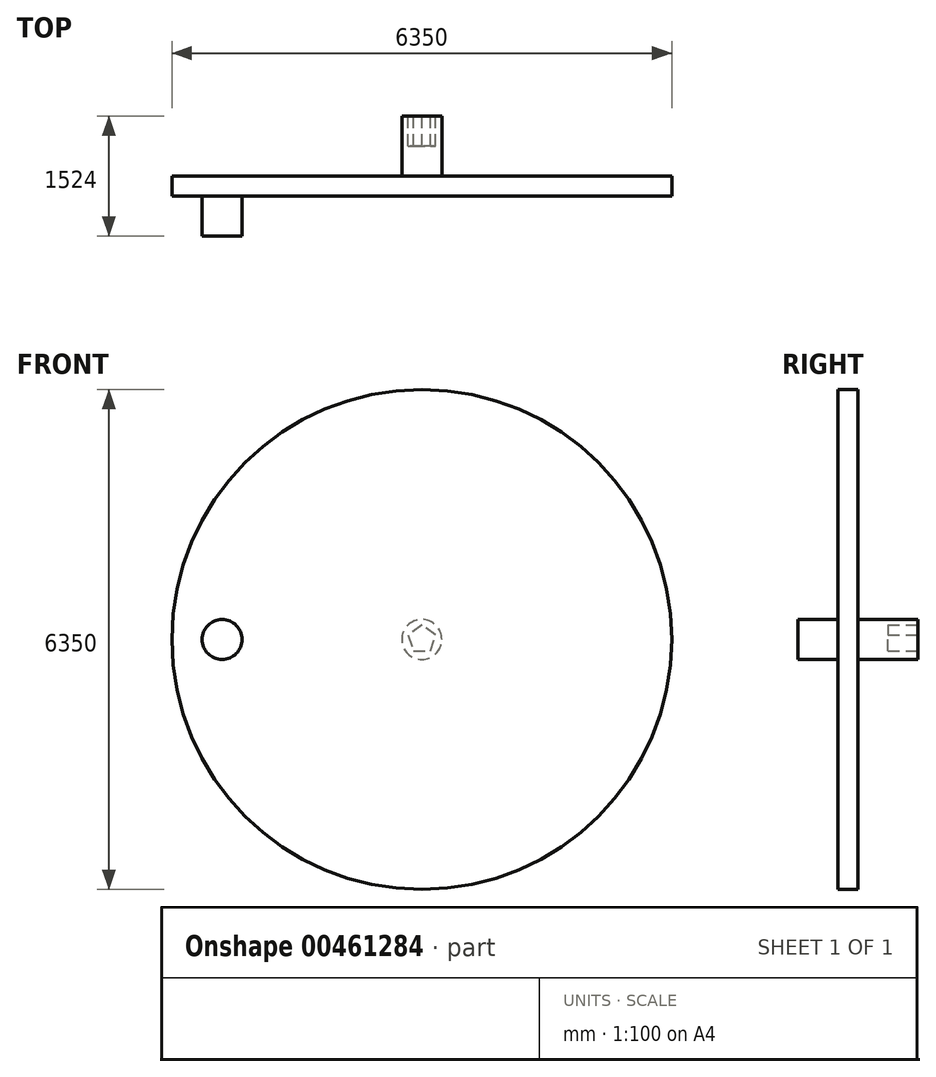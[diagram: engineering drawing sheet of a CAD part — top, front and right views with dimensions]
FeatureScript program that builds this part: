
annotation { "Feature Type Name" : "Feature", "Feature Type Description" : "" }
export const myFeature = defineFeature(function(context is Context, id is Id, definition is map)
    precondition{}
    {
        {
            var Q0;
            Q0=qCreatedBy(makeId("Front.planeOp"),FACE);
            var sketch = newSketch(context, id + "F0", { "sketchPlane" : qUnion([Q0])});
            skCircle(sketch, "E0", {"center": v(0, 0) * mm, "radius": 3175 * mm});
            skSolve(sketch);
        }
        {
            var Q0;
            Q0 = qSketchRegion(id + "F0", true);
            extrude(context, id + "F1", {"entities" : qUnion([Q0]), "endBound" : BoundingType.SYMMETRIC, "depth" : 254 * mm});
        }
        {
            var Q0;
            Q0=makeQuery(id+"F1.opExtrude","CAP_FACE",FACE,{"disambiguationData":[OSD([sQuery(id+"F0.wireOp",EDGE,"E0")])],"isStart":false});
            var sketch = newSketch(context, id + "F2", { "sketchPlane" : qUnion([Q0])});
            skCircle(sketch, "E1", {"center": v(-2536.95, 0) * mm, "radius": 254 * mm});
            skSolve(sketch);
        }
        {
            var Q0;
            Q0=makeQuery(id+"F2.imprint","IMPRINT",FACE,{"disambiguationData":[TD([[makeQuery(id+"F2.imprint","IMPRINT",EDGE,{"derivedFrom":sQuery(id+"F2.wireOp",EDGE,"E1")}),1.0]])]});
            var Q1;
            Q1 = qSketchRegion(id + "F4", true);
            extrude(context, id + "F3", {"entities" : qUnion([Q0, Q1]), "operationType" : NewBodyOperationType.ADD, "depth" : 508 * mm});
        }
        {
            var Q0;
            Q0=makeQuery(id+"F1.opExtrude","CAP_FACE",FACE,{"disambiguationData":[OSD([sQuery(id+"F0.wireOp",EDGE,"E0")])],"isStart":true});
            var sketch = newSketch(context, id + "F4", { "sketchPlane" : qUnion([Q0])});
            skCircle(sketch, "E2", {"center": v(0, 0) * mm, "radius": 254 * mm});
            skSolve(sketch);
        }
        {
            var Q0;
            Q0 = qSketchRegion(id + "F4", true);
            extrude(context, id + "F5", {"entities" : qUnion([Q0]), "operationType" : NewBodyOperationType.ADD, "depth" : 762 * mm});
        }
        {
            var Q0;
            Q0=makeQuery(id+"F5.opExtrude","CAP_FACE",FACE,{"disambiguationData":[OSD([sQuery(id+"F4.wireOp",EDGE,"E2")])],"isStart":false});
            var sketch = newSketch(context, id + "F6", { "sketchPlane" : qUnion([Q0])});
            skCircle(sketch, "E3.cCircle", {"center": v(0, 0) * mm, "radius": 182.65 * mm, "construction": true});
            skLineSegment(sketch, "E3.0", {"start": v(0, 182.65) * mm, "end": v(173.7, 56.44) * mm});
            skLineSegment(sketch, "E3.1", {"start": v(173.7, 56.44) * mm, "end": v(107.36, -147.76) * mm});
            skLineSegment(sketch, "E3.2", {"start": v(107.36, -147.76) * mm, "end": v(-107.36, -147.76) * mm});
            skLineSegment(sketch, "E3.3", {"start": v(-107.36, -147.76) * mm, "end": v(-173.7, 56.44) * mm});
            skLineSegment(sketch, "E3.4", {"start": v(-173.7, 56.44) * mm, "end": v(0, 182.65) * mm});
            skSolve(sketch);
        }
        {
            var Q0;
            Q0=makeQuery(id+"F6.imprint","IMPRINT",FACE,{"disambiguationData":[TD([[makeQuery(id+"F6.imprint","IMPRINT",EDGE,{"derivedFrom":sQuery(id+"F6.wireOp",EDGE,"E3.0")}),-1.0]])]});
            extrude(context, id + "F7", {"entities" : qUnion([Q0]), "operationType" : NewBodyOperationType.REMOVE, "oppositeDirection" : true, "depth" : 381 * mm});
        }
    });
